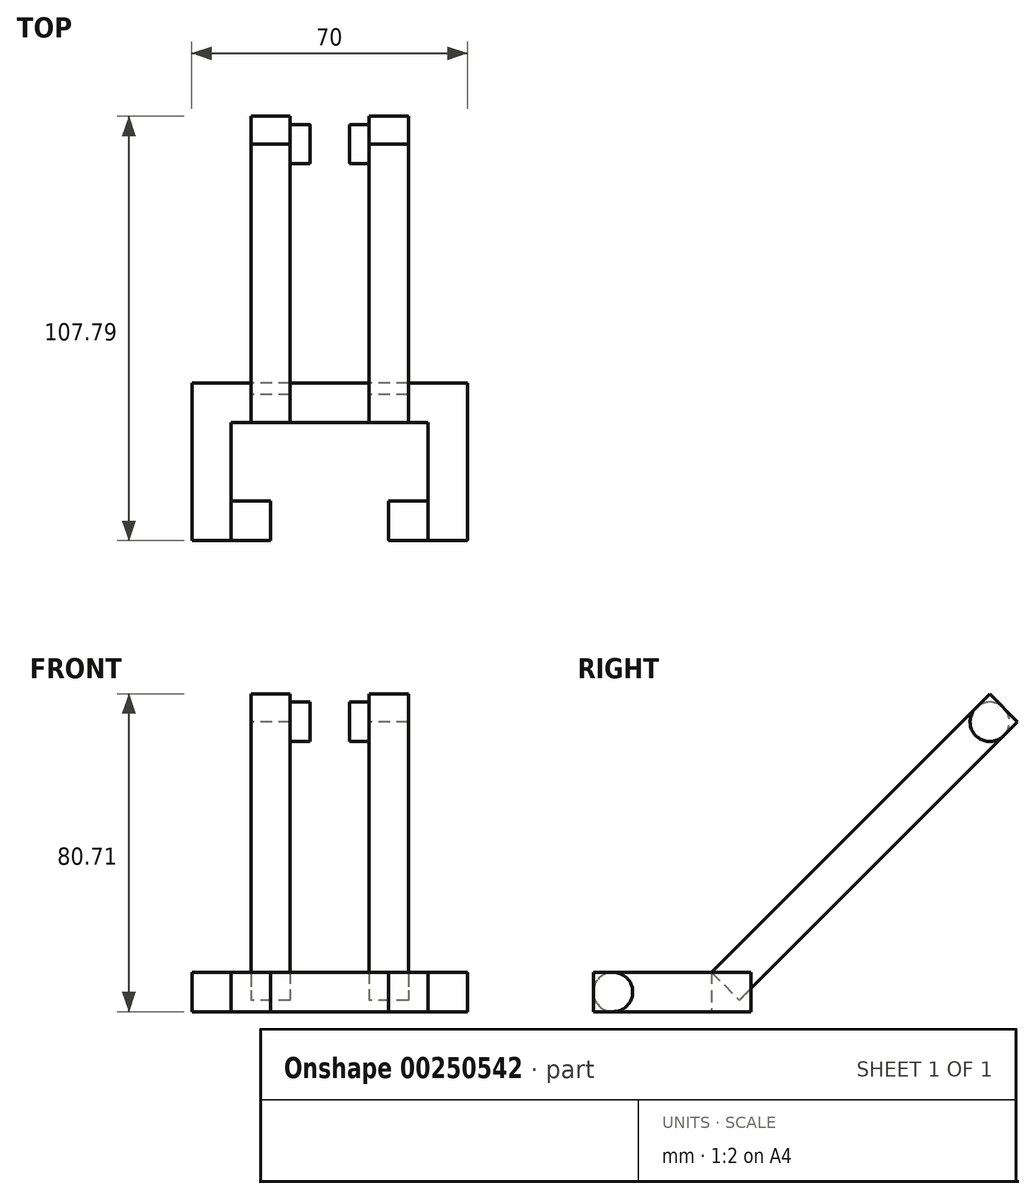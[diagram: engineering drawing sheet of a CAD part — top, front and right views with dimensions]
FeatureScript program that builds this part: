
annotation { "Feature Type Name" : "Feature", "Feature Type Description" : "" }
export const myFeature = defineFeature(function(context is Context, id is Id, definition is map)
    precondition{}
    {
        {
            var Q0;
            Q0=qCreatedBy(makeId("Top.planeOp"),FACE);
            var sketch = newSketch(context, id + "F0", { "sketchPlane" : qUnion([Q0])});
            skLineSegment(sketch, "E0", {"start": v(-23.82, -22.04) * mm, "end": v(-23.82, 17.96) * mm});
            skLineSegment(sketch, "E1", {"start": v(-23.82, 17.96) * mm, "end": v(11.18, 17.96) * mm});
            skLineSegment(sketch, "E2", {"start": v(11.18, 17.96) * mm, "end": v(11.18, -59.24) * mm, "construction": true});
            skLineSegment(sketch, "E3", {"start": v(-13.82, -12.04) * mm, "end": v(-13.82, 7.96) * mm});
            skLineSegment(sketch, "E4", {"start": v(-13.82, 7.96) * mm, "end": v(11.18, 7.96) * mm});
            skLineSegment(sketch, "E5", {"start": v(-13.82, -12.04) * mm, "end": v(-13.82, -22.04) * mm});
            skLineSegment(sketch, "E6", {"start": v(-23.82, -22.04) * mm, "end": v(-13.82, -22.04) * mm});
            skLineSegment(sketch, "E7.MirrorCS", {"start": v(36.18, 7.96) * mm, "end": v(11.18, 7.96) * mm});
            skLineSegment(sketch, "E8.MirrorCS", {"start": v(46.18, 17.96) * mm, "end": v(11.18, 17.96) * mm});
            skLineSegment(sketch, "E9.MirrorCS", {"start": v(46.18, -22.04) * mm, "end": v(46.18, 17.96) * mm});
            skLineSegment(sketch, "E10.MirrorCS", {"start": v(46.18, -22.04) * mm, "end": v(36.18, -22.04) * mm});
            skLineSegment(sketch, "E11.MirrorCS", {"start": v(36.18, -12.04) * mm, "end": v(36.18, -22.04) * mm});
            skLineSegment(sketch, "E12.MirrorCS", {"start": v(36.18, -12.04) * mm, "end": v(36.18, 7.96) * mm});
            skSolve(sketch);
        }
        {
            var Q0;
            Q0=makeQuery(id+"F0.imprint","IMPRINT",FACE,{"disambiguationData":[TD([[makeQuery(id+"F0.imprint","IMPRINT",EDGE,{"derivedFrom":sQuery(id+"F0.wireOp",EDGE,"E0")}),-1.0]])]});
            extrude(context, id + "F1", {"entities" : qUnion([Q0]), "depth" : 10 * mm});
        }
        {
            var Q0;
            Q0=makeQuery(id+"F1.opExtrude","SWEPT_FACE",FACE,{"disambiguationData":[OSD([sQuery(id+"F0.wireOp",EDGE,"E3"),sQuery(id+"F0.wireOp",EDGE,"E5")])]});
            var sketch = newSketch(context, id + "F2", { "sketchPlane" : qUnion([Q0])});
            skLineSegment(sketch, "E13", {"start": v(-22.04, 5) * mm, "end": v(-17.04, 5) * mm, "construction": true});
            skCircle(sketch, "E14", {"center": v(-17.04, 5) * mm, "radius": 5 * mm});
            skSolve(sketch);
        }
        {
            var Q0;
            {var subQ0=sQuery(id+"F2.wireOp",EDGE,"E14");var subQ1=sQuery(id+"F0.wireOp",EDGE,"E5");var subQ2=makeQuery(id+"F2.imprint","INTERSECT",VERTEX,{"derivedFrom":[makeQuery(id+"F1.opExtrude","SWEPT_EDGE",EDGE,{"disambiguationData":[OSD([subQ1,sQuery(id+"F0.wireOp",EDGE,"E6")])]}),subQ0]});Q0=makeQuery(id+"F2.imprint","IMPRINT",FACE,{"disambiguationData":[TD([[makeQuery(id+"F2.imprint","IMPRINT",EDGE,{"disambiguationData":[TD([[subQ2,1.0]])],"derivedFrom":subQ0}),1.0]])]});}
            extrude(context, id + "F3", {"entities" : qUnion([Q0]), "operationType" : NewBodyOperationType.ADD, "depth" : 10 * mm});
        }
        {
            var Q0;
            Q0=makeQuery(id+"F1.opExtrude","SWEPT_FACE",FACE,{"disambiguationData":[OSD([sQuery(id+"F0.wireOp",EDGE,"E11.MirrorCS"),sQuery(id+"F0.wireOp",EDGE,"E12.MirrorCS")])]});
            var sketch = newSketch(context, id + "F4", { "sketchPlane" : qUnion([Q0])});
            skLineSegment(sketch, "E15", {"start": v(22.04, 5) * mm, "end": v(17.04, 5) * mm, "construction": true});
            skCircle(sketch, "E16", {"center": v(17.04, 5) * mm, "radius": 5 * mm});
            skSolve(sketch);
        }
        {
            var Q0;
            {var subQ0=sQuery(id+"F4.wireOp",EDGE,"E16");var subQ1=sQuery(id+"F0.wireOp",EDGE,"E12.MirrorCS");var subQ2=sQuery(id+"F0.wireOp",EDGE,"E11.MirrorCS");var subQ3=makeQuery(id+"F4.imprint","INTERSECT",VERTEX,{"derivedFrom":[makeQuery(id+"F1.opExtrude","CAP_EDGE",EDGE,{"disambiguationData":[OSD([subQ2,subQ1])],"isStart":false}),subQ0]});Q0=makeQuery(id+"F4.imprint","IMPRINT",FACE,{"disambiguationData":[TD([[makeQuery(id+"F4.imprint","IMPRINT",EDGE,{"disambiguationData":[TD([[subQ3,1.0]])],"derivedFrom":subQ0}),1.0]])]});}
            var Q1;
            Q1=sQuery(id+"F4.wireOp",EDGE,"E16");
            extrude(context, id + "F5", {"entities" : qUnion([Q0]), "operationType" : NewBodyOperationType.ADD, "surfaceEntities" : qUnion([Q1]), "depth" : 10 * mm});
        }
        {
            var Q0;
            Q0=makeQuery(id+"F1.opExtrude","CAP_EDGE",EDGE,{"disambiguationData":[OSD([sQuery(id+"F0.wireOp",EDGE,"E1"),sQuery(id+"F0.wireOp",EDGE,"E8.MirrorCS")])],"isStart":true});
            cPlane(context, id + "F6", {"entities" : qUnion([Q0]), "cplaneType" : CPlaneType.LINE_ANGLE, "offset" : 25 * mm, "angle" : 45 * degree, "oppositeDirection" : true, "width" : 150 * mm, "height" : 150 * mm});
        }
        {
            var Q0;
            Q0=qCreatedBy(id+"F6.planeOp",FACE);
            var sketch = newSketch(context, id + "F7", { "sketchPlane" : qUnion([Q0])});
            skLineSegment(sketch, "E17.bottom", {"start": v(31.18, 1.44) * mm, "end": v(21.18, 1.44) * mm});
            skLineSegment(sketch, "E17.top", {"start": v(31.18, -8.56) * mm, "end": v(21.18, -8.56) * mm});
            skLineSegment(sketch, "E17.left", {"start": v(31.18, 1.44) * mm, "end": v(31.18, -8.56) * mm});
            skLineSegment(sketch, "E17.right", {"start": v(21.18, 1.44) * mm, "end": v(21.18, -8.56) * mm});
            skLineSegment(sketch, "E18.bottom", {"start": v(1.18, 1.44) * mm, "end": v(-8.82, 1.44) * mm});
            skLineSegment(sketch, "E18.top", {"start": v(1.18, -8.56) * mm, "end": v(-8.82, -8.56) * mm});
            skLineSegment(sketch, "E18.left", {"start": v(1.18, 1.44) * mm, "end": v(1.18, -8.56) * mm});
            skLineSegment(sketch, "E18.right", {"start": v(-8.82, 1.44) * mm, "end": v(-8.82, -8.56) * mm});
            skSolve(sketch);
        }
        {
            var Q0;
            Q0 = qSketchRegion(id + "F7", true);
            var Q1;
            Q1=sQuery(id+"F7.wireOp",EDGE,"E18.left");
            var Q2;
            Q2=sQuery(id+"F7.wireOp",EDGE,"E18.top");
            var Q3;
            Q3=sQuery(id+"F7.wireOp",EDGE,"E18.bottom");
            var Q4;
            Q4=sQuery(id+"F7.wireOp",EDGE,"E18.right");
            var Q5;
            Q5=sQuery(id+"F7.wireOp",EDGE,"E17.right");
            var Q6;
            Q6=sQuery(id+"F7.wireOp",EDGE,"E17.top");
            var Q7;
            Q7=sQuery(id+"F7.wireOp",EDGE,"E17.left");
            var Q8;
            Q8=sQuery(id+"F7.wireOp",EDGE,"E17.bottom");
            extrude(context, id + "F8", {"entities" : qUnion([Q0]), "surfaceEntities" : qUnion([Q1, Q2, Q3, Q4, Q5, Q6, Q7, Q8]), "oppositeDirection" : true, "depth" : 100 * mm});
        }
        {
            var Q0;
            Q0=makeQuery(id+"F8.opExtrude","SWEPT_FACE",FACE,{"disambiguationData":[OSD([sQuery(id+"F7.wireOp",EDGE,"E18.left")])]});
            var sketch = newSketch(context, id + "F9", { "sketchPlane" : qUnion([Q0])});
            skLineSegment(sketch, "E19", {"start": v(82.21, 77.18) * mm, "end": v(78.68, 73.64) * mm, "construction": true});
            skCircle(sketch, "E20", {"center": v(78.68, 73.64) * mm, "radius": 5 * mm});
            skSolve(sketch);
        }
        {
            var Q0;
            {var subQ0=sQuery(id+"F9.wireOp",EDGE,"E20");var subQ1=sQuery(id+"F7.wireOp",EDGE,"E18.left");var subQ3=makeQuery(id+"F9.imprint","INTERSECT",VERTEX,{"derivedFrom":[makeQuery(id+"F8.opExtrude","CAP_EDGE",EDGE,{"disambiguationData":[OSD([subQ1])],"isStart":false}),subQ0]});Q0=makeQuery(id+"F9.imprint","IMPRINT",FACE,{"disambiguationData":[TD([[makeQuery(id+"F9.imprint","IMPRINT",EDGE,{"disambiguationData":[TD([[subQ3,-1.0]])],"derivedFrom":subQ0}),1.0]])]});}
            extrude(context, id + "F10", {"entities" : qUnion([Q0]), "operationType" : NewBodyOperationType.ADD, "depth" : 5 * mm});
        }
        {
            var Q0;
            Q0=makeQuery(id+"F8.opExtrude","SWEPT_FACE",FACE,{"disambiguationData":[OSD([sQuery(id+"F7.wireOp",EDGE,"E17.right")])]});
            var sketch = newSketch(context, id + "F11", { "sketchPlane" : qUnion([Q0])});
            skLineSegment(sketch, "E21", {"start": v(-82.21, 77.18) * mm, "end": v(-78.68, 73.64) * mm, "construction": true});
            skCircle(sketch, "E22", {"center": v(-78.68, 73.64) * mm, "radius": 5 * mm});
            skSolve(sketch);
        }
        {
            var Q0;
            {var subQ0=sQuery(id+"F11.wireOp",EDGE,"E22");var subQ1=sQuery(id+"F7.wireOp",EDGE,"E17.right");var subQ2=makeQuery(id+"F11.imprint","INTERSECT",VERTEX,{"derivedFrom":[makeQuery(id+"F8.opExtrude","CAP_EDGE",EDGE,{"disambiguationData":[OSD([subQ1])],"isStart":false}),subQ0]});Q0=makeQuery(id+"F11.imprint","IMPRINT",FACE,{"disambiguationData":[TD([[makeQuery(id+"F11.imprint","IMPRINT",EDGE,{"disambiguationData":[TD([[subQ2,1.0]])],"derivedFrom":subQ0}),1.0]])]});}
            extrude(context, id + "F12", {"entities" : qUnion([Q0]), "operationType" : NewBodyOperationType.ADD, "depth" : 5 * mm});
        }
    });
